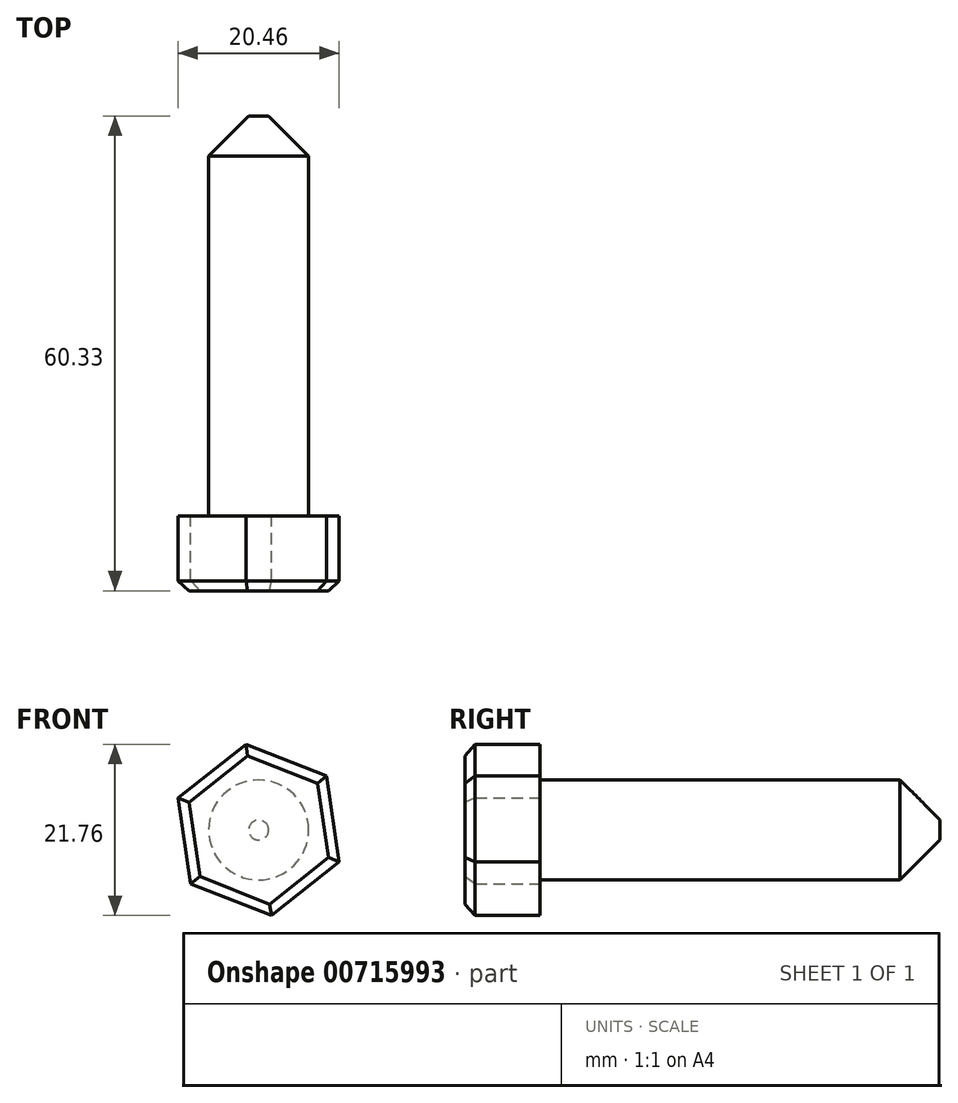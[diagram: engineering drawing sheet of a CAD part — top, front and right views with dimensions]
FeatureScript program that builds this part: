
annotation { "Feature Type Name" : "Feature", "Feature Type Description" : "" }
export const myFeature = defineFeature(function(context is Context, id is Id, definition is map)
    precondition{}
    {
        {
            var Q0;
            Q0=qCreatedBy(makeId("Front.planeOp"),FACE);
            var sketch = newSketch(context, id + "F0", { "sketchPlane" : qUnion([Q0])});
            skCircle(sketch, "E0.cCircle", {"center": v(0, 0) * mm, "radius": 9.53 * mm, "construction": true});
            skLineSegment(sketch, "E0.0", {"start": v(-10.23, 4.05) * mm, "end": v(-1.61, 10.88) * mm});
            skLineSegment(sketch, "E0.1", {"start": v(-1.61, 10.88) * mm, "end": v(8.62, 6.83) * mm});
            skLineSegment(sketch, "E0.2", {"start": v(8.62, 6.83) * mm, "end": v(10.23, -4.05) * mm});
            skLineSegment(sketch, "E0.3", {"start": v(10.23, -4.05) * mm, "end": v(1.61, -10.88) * mm});
            skLineSegment(sketch, "E0.4", {"start": v(1.61, -10.88) * mm, "end": v(-8.62, -6.83) * mm});
            skLineSegment(sketch, "E0.5", {"start": v(-8.62, -6.83) * mm, "end": v(-10.23, 4.05) * mm});
            skPoint(sketch, "E0.0.midPoint", {"position": v(-5.92, 7.46) * mm});
            skSolve(sketch);
        }
        {
            var Q0;
            Q0=makeQuery(id+"F0.imprint","IMPRINT",FACE,{"disambiguationData":[TD([[makeQuery(id+"F0.imprint","IMPRINT",EDGE,{"derivedFrom":sQuery(id+"F0.wireOp",EDGE,"E0.0")}),-1.0]])]});
            extrude(context, id + "F1", {"entities" : qUnion([Q0]), "depth" : 9.52 * mm, "offsetDistance" : 25.4 * mm});
        }
        {
            var Q0;
            Q0=makeQuery(id+"F1.opExtrude","CAP_FACE",FACE,{"disambiguationData":[OSD([sQuery(id+"F0.wireOp",EDGE,"E0.0"),sQuery(id+"F0.wireOp",EDGE,"E0.1"),sQuery(id+"F0.wireOp",EDGE,"E0.2"),sQuery(id+"F0.wireOp",EDGE,"E0.3"),sQuery(id+"F0.wireOp",EDGE,"E0.4"),sQuery(id+"F0.wireOp",EDGE,"E0.5")])],"isStart":true});
            cPlane(context, id + "F2", {"entities" : qUnion([Q0]), "cplaneType" : CPlaneType.OFFSET, "offset" : 0 * mm, "width" : 152.4 * mm, "height" : 152.4 * mm});
        }
        {
            var Q0;
            Q0=qCreatedBy(id+"F2.planeOp",FACE);
            var sketch = newSketch(context, id + "F3", { "sketchPlane" : qUnion([Q0])});
            skCircle(sketch, "E1", {"center": v(0, 0) * mm, "radius": 6.35 * mm});
            skSolve(sketch);
        }
        {
            var Q0;
            Q0=makeQuery(id+"F3.imprint","IMPRINT",FACE,{"disambiguationData":[TD([[makeQuery(id+"F3.imprint","IMPRINT",EDGE,{"derivedFrom":sQuery(id+"F3.wireOp",EDGE,"E1")}),1.0]])]});
            extrude(context, id + "F4", {"entities" : qUnion([Q0]), "operationType" : NewBodyOperationType.ADD, "depth" : 50.8 * mm, "offsetDistance" : 25.4 * mm});
        }
        {
            var Q0;
            Q0=makeQuery(id+"F4.opExtrude","CAP_EDGE",EDGE,{"disambiguationData":[OSD([sQuery(id+"F3.wireOp",EDGE,"E1")])],"isStart":false});
            chamfer(context, id + "F5", {"entities" : qUnion([Q0]), "width" : 5.08 * mm, "tangentPropagation" : true});
        }
        {
            var Q0;
            Q0=makeQuery(id+"F1.opExtrude","CAP_EDGE",EDGE,{"disambiguationData":[OSD([sQuery(id+"F0.wireOp",EDGE,"E0.0")])],"isStart":false});
            var Q1;
            Q1=makeQuery(id+"F1.opExtrude","CAP_EDGE",EDGE,{"disambiguationData":[OSD([sQuery(id+"F0.wireOp",EDGE,"E0.1")])],"isStart":false});
            var Q2;
            Q2=makeQuery(id+"F1.opExtrude","CAP_EDGE",EDGE,{"disambiguationData":[OSD([sQuery(id+"F0.wireOp",EDGE,"E0.2")])],"isStart":false});
            var Q3;
            Q3=makeQuery(id+"F1.opExtrude","CAP_EDGE",EDGE,{"disambiguationData":[OSD([sQuery(id+"F0.wireOp",EDGE,"E0.3")])],"isStart":false});
            var Q4;
            Q4=makeQuery(id+"F1.opExtrude","CAP_EDGE",EDGE,{"disambiguationData":[OSD([sQuery(id+"F0.wireOp",EDGE,"E0.4")])],"isStart":false});
            var Q5;
            Q5=makeQuery(id+"F1.opExtrude","CAP_EDGE",EDGE,{"disambiguationData":[OSD([sQuery(id+"F0.wireOp",EDGE,"E0.5")])],"isStart":false});
            chamfer(context, id + "F6", {"entities" : qUnion([Q0, Q1, Q2, Q3, Q4, Q5]), "width" : 1.27 * mm, "tangentPropagation" : true});
        }
    });
